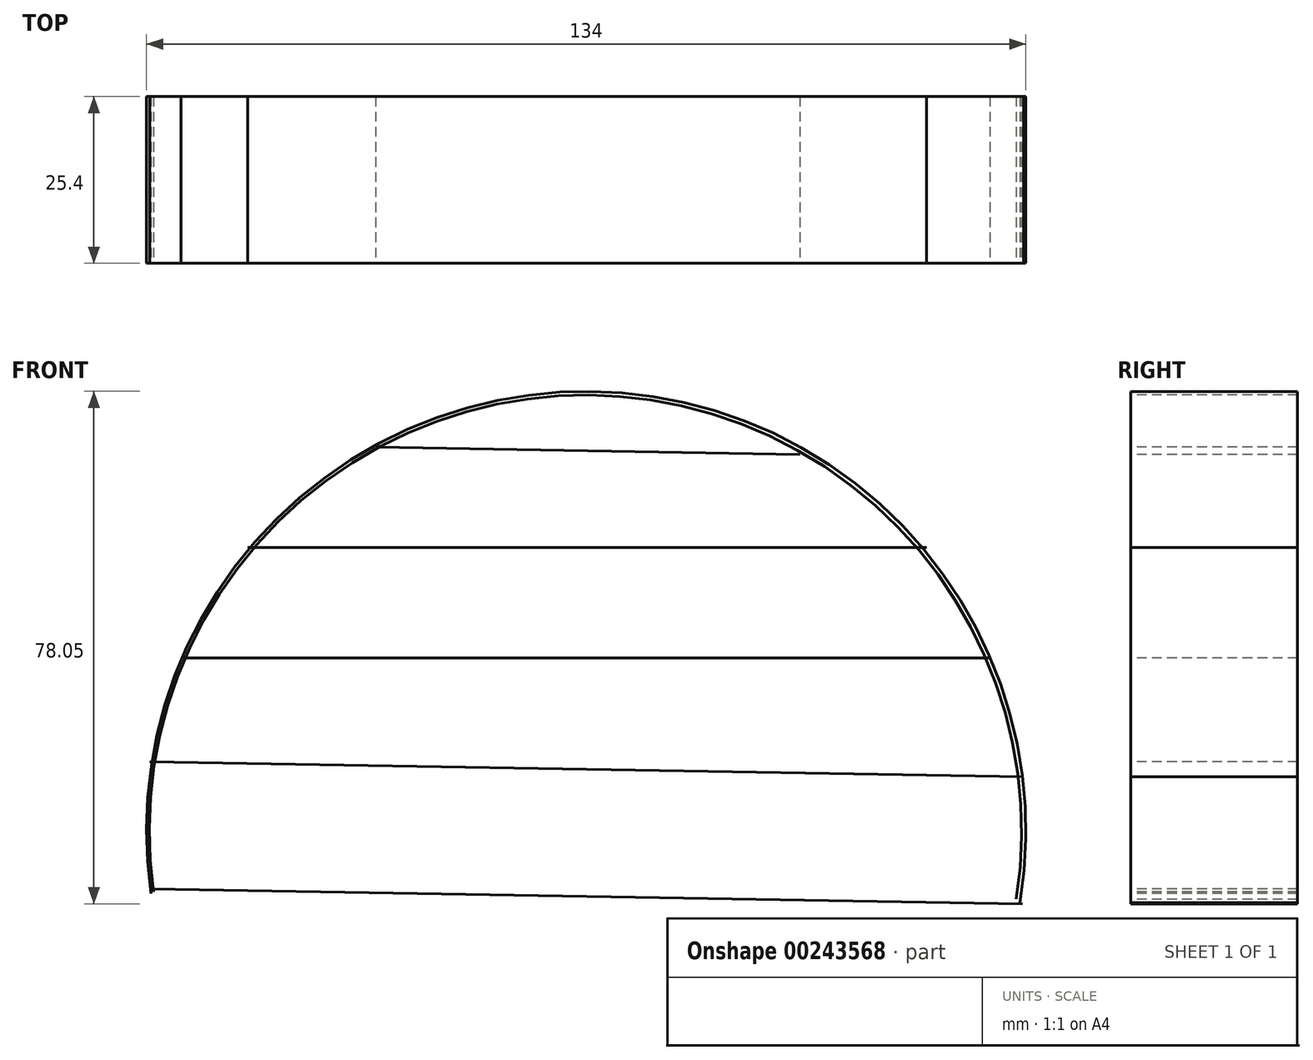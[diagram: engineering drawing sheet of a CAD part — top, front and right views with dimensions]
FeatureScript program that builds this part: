
annotation { "Feature Type Name" : "Feature", "Feature Type Description" : "" }
export const myFeature = defineFeature(function(context is Context, id is Id, definition is map)
    precondition{}
    {
        {
            var Q0;
            Q0=qCreatedBy(makeId("Front.planeOp"),FACE);
            var sketch = newSketch(context, id + "F0", { "sketchPlane" : qUnion([Q0])});
            skArc(sketch, "E0", {"start": v(67.71, -41.37) * mm, "mid": v(2.31, 36.5) * mm, "end": v(-64.73, -39.97) * mm});
            skSolve(sketch);
        }
        {
            var Q0;
            Q0=sQuery(id+"F0.wireOp",EDGE,"E0");
            extrude(context, id + "F1", {"bodyType" : ToolBodyType.SURFACE, "surfaceEntities" : qUnion([Q0]), "depth" : 25.4 * mm});
        }
        {
            var Q0;
            Q0=qCreatedBy(makeId("Front.planeOp"),FACE);
            var sketch = newSketch(context, id + "F2", { "sketchPlane" : qUnion([Q0])});
            skLineSegment(sketch, "E1", {"start": v(-64.73, -39.26) * mm, "end": v(68.07, -41.55) * mm});
            skLineSegment(sketch, "E2", {"start": v(-64.9, -19.94) * mm, "end": v(68.24, -22.23) * mm});
            skLineSegment(sketch, "E3", {"start": v(-60.16, -4.13) * mm, "end": v(63.15, -4.13) * mm});
            skLineSegment(sketch, "E4", {"start": v(-49.97, 12.73) * mm, "end": v(53.49, 12.73) * mm});
            skLineSegment(sketch, "E5", {"start": v(-30.48, 28.01) * mm, "end": v(34.15, 26.9) * mm});
            skSolve(sketch);
        }
        {
            var Q0;
            Q0=sQuery(id+"F2.wireOp",EDGE,"E5");
            var Q1;
            Q1=sQuery(id+"F2.wireOp",EDGE,"E4");
            var Q2;
            Q2=sQuery(id+"F2.wireOp",EDGE,"E3");
            var Q3;
            Q3=sQuery(id+"F2.wireOp",EDGE,"E2");
            var Q4;
            Q4=sQuery(id+"F2.wireOp",EDGE,"E1");
            extrude(context, id + "F3", {"bodyType" : ToolBodyType.SURFACE, "surfaceEntities" : qUnion([Q0, Q1, Q2, Q3, Q4]), "depth" : 25.4 * mm});
        }
        {
            var Q0;
            Q0=qCreatedBy(makeId("Front.planeOp"),FACE);
            var sketch = newSketch(context, id + "F4", { "sketchPlane" : qUnion([Q0])});
            skArc(sketch, "E6", {"start": v(67.14, -40.84) * mm, "mid": v(2.05, 35.93) * mm, "end": v(-64.34, -39.73) * mm});
            skSolve(sketch);
        }
        {
            var Q0;
            Q0=sQuery(id+"F4.wireOp",EDGE,"E6");
            extrude(context, id + "F5", {"bodyType" : ToolBodyType.SURFACE, "surfaceEntities" : qUnion([Q0]), "depth" : 25.4 * mm});
        }
    });
